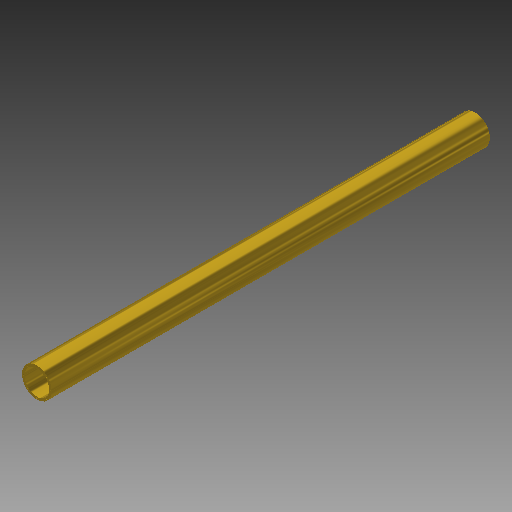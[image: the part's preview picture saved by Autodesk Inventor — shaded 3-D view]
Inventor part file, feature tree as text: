
AUTODESK INVENTOR PART (.ipt)
format: ipt  version: 2017 (Build 210142000, 142)  size: 132,608 bytes
history: native  units: mm (DEFAULTED — no unit token found)
features: sketch x3, revolve x2, pattern_circular x2, extrude x1
ambient origin geometry x8: Origin, YZ Plane, XZ Plane, XY Plane, X Axis, Y Axis, Z Axis, Center Point
bodies: Solid1 (feature_tree)
feature tree (8):
  extrude  "Extrusion1"  Depth=36.5mm
  revolve  "Revolution1"  [1 undecoded]
  pattern_circular  "Circular Pattern2"  Angle=90.0deg  [1 undecoded]
  revolve  "Revolution2"  Angle=360.0deg
  pattern_circular  "Circular Pattern3"  [2 undecoded]
  sketch  "Sketch1"  dims[d0=30.5mm d1=36.5mm]
  sketch  "Sketch2"  dims[d2=539.8mm d3=0.0mm d4=2.0mm]
  sketch  "Sketch3"  dims[d5=0.5mm d6=90.0deg d10=80.0mm d11=360.0deg d13=2.0mm d14=0.5mm d15=90.0deg d16=80.0mm d17=360.0deg]
note: 4 required parameter values undecoded (feature->parameter linkage not recoverable at this tier; creation-order binding heuristic only, values carry confidence <= 0.55)